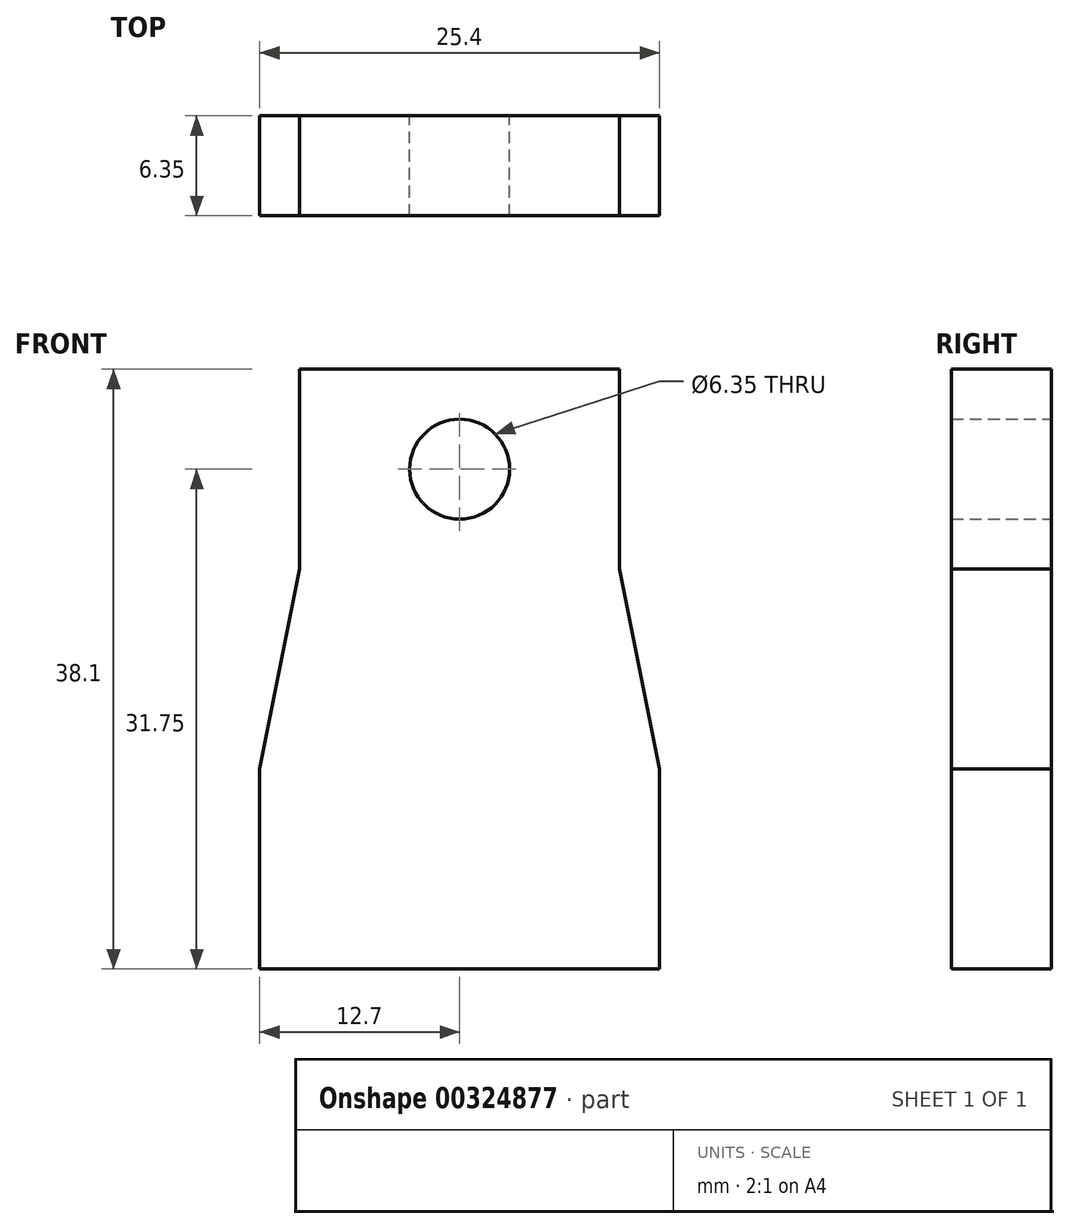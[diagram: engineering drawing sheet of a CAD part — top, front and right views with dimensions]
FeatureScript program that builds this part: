
annotation { "Feature Type Name" : "Feature", "Feature Type Description" : "" }
export const myFeature = defineFeature(function(context is Context, id is Id, definition is map)
    precondition{}
    {
        {
            var Q0;
            Q0=qCreatedBy(makeId("Front.planeOp"),FACE);
            var sketch = newSketch(context, id + "F0", { "sketchPlane" : qUnion([Q0])});
            skLineSegment(sketch, "E0", {"start": v(0, 0) * mm, "end": v(25.4, 0) * mm});
            skLineSegment(sketch, "E1", {"start": v(0, 0) * mm, "end": v(0, 12.7) * mm});
            skLineSegment(sketch, "E2", {"start": v(0, 12.7) * mm, "end": v(2.54, 25.4) * mm});
            skLineSegment(sketch, "E3", {"start": v(2.54, 25.4) * mm, "end": v(2.54, 38.1) * mm});
            skLineSegment(sketch, "E4", {"start": v(12.7, 0) * mm, "end": v(12.7, 1.97) * mm});
            skPoint(sketch, "E4.endSnap0", {"position": v(12.7, 0) * mm});
            skLineSegment(sketch, "E5.MirrorCS", {"start": v(22.86, 25.4) * mm, "end": v(22.86, 38.1) * mm});
            skLineSegment(sketch, "E6.MirrorCS", {"start": v(25.4, 0) * mm, "end": v(25.4, 12.7) * mm});
            skLineSegment(sketch, "E7.MirrorCS", {"start": v(25.4, 12.7) * mm, "end": v(22.86, 25.4) * mm});
            skLineSegment(sketch, "E8", {"start": v(2.54, 38.1) * mm, "end": v(22.86, 38.1) * mm});
            skLineSegment(sketch, "E9", {"start": v(12.7, 0) * mm, "end": v(12.7, 31.75) * mm});
            skPoint(sketch, "E9.endSnap0", {"position": v(2.54, 31.75) * mm});
            skCircle(sketch, "E10", {"center": v(12.7, 31.75) * mm, "radius": 3.18 * mm});
            skSolve(sketch);
        }
        {
            var Q0;
            Q0 = qSketchRegion(id + "F0", true);
            extrude(context, id + "F1", {"entities" : qUnion([Q0]), "depth" : 6.35 * mm});
        }
    });
